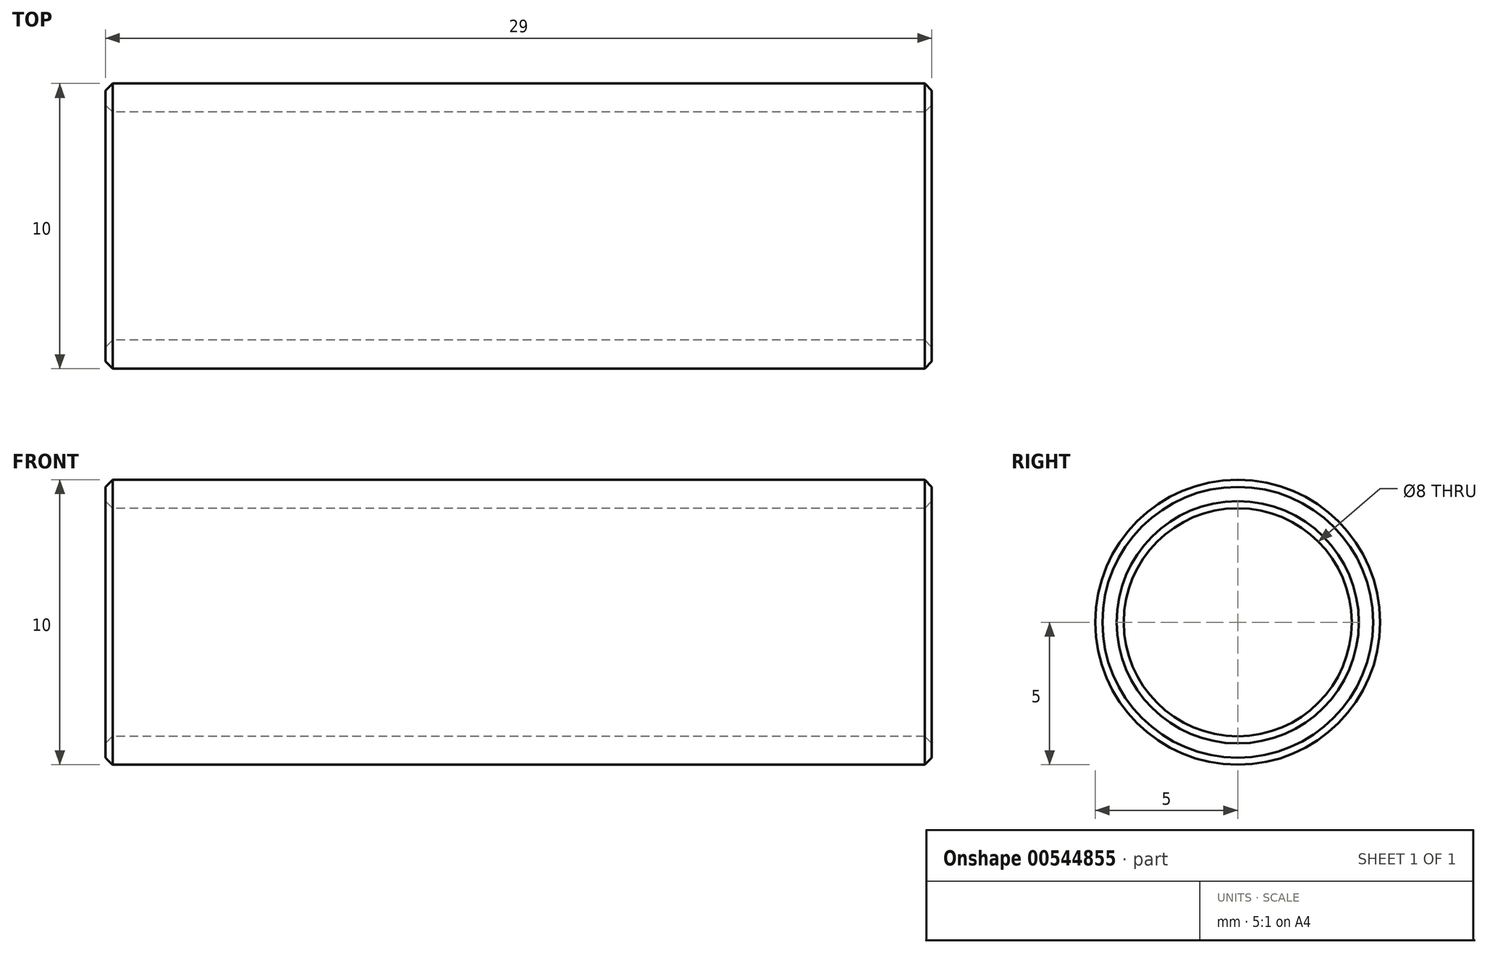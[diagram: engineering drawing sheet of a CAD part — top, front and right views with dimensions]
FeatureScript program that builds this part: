
annotation { "Feature Type Name" : "Feature", "Feature Type Description" : "" }
export const myFeature = defineFeature(function(context is Context, id is Id, definition is map)
    precondition{}
    {
        {
            var Q0;
            Q0=qCreatedBy(makeId("Right.planeOp"),FACE);
            var sketch = newSketch(context, id + "F0", { "sketchPlane" : qUnion([Q0])});
            skCircle(sketch, "E0", {"center": v(0, 0) * mm, "radius": 4 * mm});
            skCircle(sketch, "E1", {"center": v(0, 0) * mm, "radius": 5 * mm});
            skSolve(sketch);
        }
        {
            var Q0;
            Q0 = qSketchRegion(id + "F0", true);
            extrude(context, id + "F1", {"entities" : qUnion([Q0]), "depth" : 29 * mm, "offsetDistance" : 25 * mm});
        }
        {
            var Q0;
            Q0=makeQuery(id+"F1.opExtrude","CAP_EDGE",EDGE,{"disambiguationData":[OSD([sQuery(id+"F0.wireOp",EDGE,"E1")])],"isStart":false});
            var Q1;
            Q1=makeQuery(id+"F1.opExtrude","CAP_EDGE",EDGE,{"disambiguationData":[OSD([sQuery(id+"F0.wireOp",EDGE,"E1")])],"isStart":true});
            var Q2;
            Q2=makeQuery(id+"F1.opExtrude","CAP_EDGE",EDGE,{"disambiguationData":[OSD([sQuery(id+"F0.wireOp",EDGE,"E0")])],"isStart":true});
            var Q3;
            Q3=makeQuery(id+"F1.opExtrude","CAP_EDGE",EDGE,{"disambiguationData":[OSD([sQuery(id+"F0.wireOp",EDGE,"E0")])],"isStart":false});
            chamfer(context, id + "F2", {"entities" : qUnion([Q0, Q1, Q2, Q3]), "width" : 0.25 * mm, "tangentPropagation" : true});
        }
    });
